# Revit family: XL_CleanerSink
name_source: partatom
category: Plumbing Fixtures
units: mm (PartAtom-declared; Revit-internal decimal feet)

## family parameters
Always vertical = Yes
Cut with Voids When Loaded = No
OmniClass Number = 23.45.00.00
OmniClass Title = Sanitary, Laundry, and Cleaning Equipment
Part Type = Normal
Room Calculation Point = No
Round Connector Dimension = Use Diameter
Shared = No
Work Plane-Based = Yes

## types (6) — shared parameters
Assembly = Pressed
Brand = Mercer
Default Elevation = 1219 mm
Description = NZ Made Cleaner Sink
Finish = Classic
Includes = Brackets
Material = 0.8mm 304 Stainless Steel
Model = XL Cleaner Sink
Rubber = Rubber
Sink Material = Stainless Steel
Waste = P&W 40mm outlet

## per-type parameters (varying)
| type | Grid | Manufacturer | Upstand |
| XLPK1 | No | Mercer | XL_CleanerSink_Upstand |
| XLPK2 | Yes | Mercer | XL_CleanerSink_Upstand |
| XLPK3-R | No | Mercer | XL_CleanerSink_UpstandExtra_R |
| XLPK3-L | No | Mercer | XL_CleanerSink_UpstandExtra_L |
| XLPK4-R | Yes |  | XL_CleanerSink_UpstandExtra_R |
| XLPK4-L | Yes | Mercer | XL_CleanerSink_UpstandExtra_L |

## geometry (parser evidence)
native form markers: Sweep x28
no freeform markers — native parametric forms only
